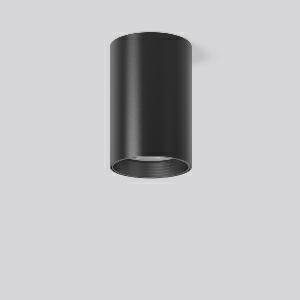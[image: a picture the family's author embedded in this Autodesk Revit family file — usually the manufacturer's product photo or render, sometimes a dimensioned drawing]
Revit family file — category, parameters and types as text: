
# Revit family: heledon_maxi_a_931227_003_2_251a
name_source: partatom
category: Lighting Fixtures
units: mm (PartAtom-declared; Revit-internal decimal feet)

## family parameters
Cut with Voids When Loaded = No
Host = Face
Light Source = No
Part Type = Normal
Room Calculation Point = No
Round Connector Dimension = Use Diameter
Shared = No

## types (1)
- HELEDON maxi A (1 x LED Modul 927, 3500 lm, 2700)
    Apparent Load = 35 VA
    Approval mark = CE
    CIE Flux Codes = 97 100 100 100 100
    Color Rendering = 92
    Color Temperature = 2700
    Default Elevation = 1800 mm
    Description = Series: HELEDON maxi
Cylindrical surface-mounted downlight. Housing: die-cast aluminium, powder-coated. Internal ceiling frame polycarbonate with bayonet mounting. Black plastic ring and recessed LED to prevent glare from the side. Optical assembly with lens made of plastic (polycarbonate) for the best homogeneous light distribution - can be changed without tools. Best colour rendering index Ra>90. Suitable for Ceiling mounting. Easy installation with a separate ceiling frame with bayonet mounting and plug connection. Driver integrated. Connected via plug-in connector. High quality converter without flickering and stroboscopic effect. The following accessories can be mounted without use of tools: interchangeable lenses, decorative glasses, honeycomb louvre, clear and frosted diffusers, white interchangeable plastic ring. 
Colour: deep black, matt (RAL 9005)
Diameter: 123 mm
Height: 183 mm
Lamp: LED
Socket: without socket
Colour temperature: 2700K
Colour rendering index (CRI): 92
System power: 35 W
Rated luminous flux: 3500 lm
Luminous efficiency: 100 lm/W
Control gear: Regulated power supply
Protection class: I
Type of protection: IP 20
    Height = 183 mm
    Lamp = 1 x LED Modul 927
    Lamp Light Flux = 3500 lm
    Lamp count = 1
    Length = 123 mm
    Lifetime = 50000 h
    Luminous efficacy = 100 lm/W
    Manufacturer = RZB
    ModVariant = No
    Model = 931227.003.2
    Mounting Place = Ceiling
    Mounting Type = Surface mounted
    Number of Poles = 1
    OnlyDefault = Yes
    Power Factor = 1
    Product Name = HELEDON maxi A
    Product group = Surface mounted downlights
    ProductGroupID = 302
    Protection Class = Protection class I
    Protection Degree = IP 20
    RLX_Detail_Level = 1
    RLX_Emergency_Light_Flux = 0 lm
    RLX_Emergency_Type = 0
    RLX_Emergency_Type_DB = No
    RlxData = <blob elided: 95781 chars, md5=5240c3fc>
    Socket = socket
    Standby Power = 0 W
    System Light Flux = 3500 lm
    System Power = 35 W
    Type Comments = Product without accessories
    Type Image = 931193.003.jpg
    URL = http://relux.com
    VarID = ---
    Voltage = 230 V
    Voltage Range = 220-240 V
    Weight = 0.00 kg
    Width = 0 mm  [stored 0 ft]

note: [stored X ft] marks values corroborated as IEEE doubles in the binary element streams (Revit-internal decimal feet)

## geometry (parser evidence)
native form markers: Blend x4, Sweep x10
no freeform markers — native parametric forms only
